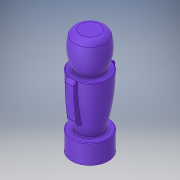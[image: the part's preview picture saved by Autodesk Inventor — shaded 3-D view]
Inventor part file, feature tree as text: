
AUTODESK INVENTOR PART (.ipt)
format: ipt  version: 2018 (Build 220112000, 112)  size: 473,088 bytes
history: native  units: in
note: dims shown in document units (in); Inventor stores cm internally (conversion verified against a paired STEP export)
features: fillet x4, sketch x2, revolve x1, extrude x1
ambient origin geometry x8: Origin, YZ Plane, XZ Plane, XY Plane, X Axis, Y Axis, Z Axis, Center Point
bodies: Solid1 (feature_tree)
feature tree (8):
  revolve  "Revolution1"  [1 undecoded]
  extrude  "Extrusion1"  Depth=0.82in
  fillet  "Fillet1"  Radius=0.1125in
  fillet  "Fillet2"  Radius=0.54in
  fillet  "Fillet3"  Radius=0.22in
  fillet  "Fillet4"  Radius=0.1in
  sketch  "Sketch1"  dims[d0=0.29in d1=0.305in]
  sketch  "Sketch2"  dims[d2=0.1125in d3=0.82in d4=0.1125in d5=0.54in d6=0.22in d7=0.1in d8=0.01in d9=90.0deg d10=0.05in d11=0.05in d12=0.15in d13=0.0in d14=0.05in d15=0.1in d16=0.01in d17=0.01in]
note: 1 required parameter value undecoded (feature->parameter linkage not recoverable at this tier; creation-order binding heuristic only, values carry confidence <= 0.55)
